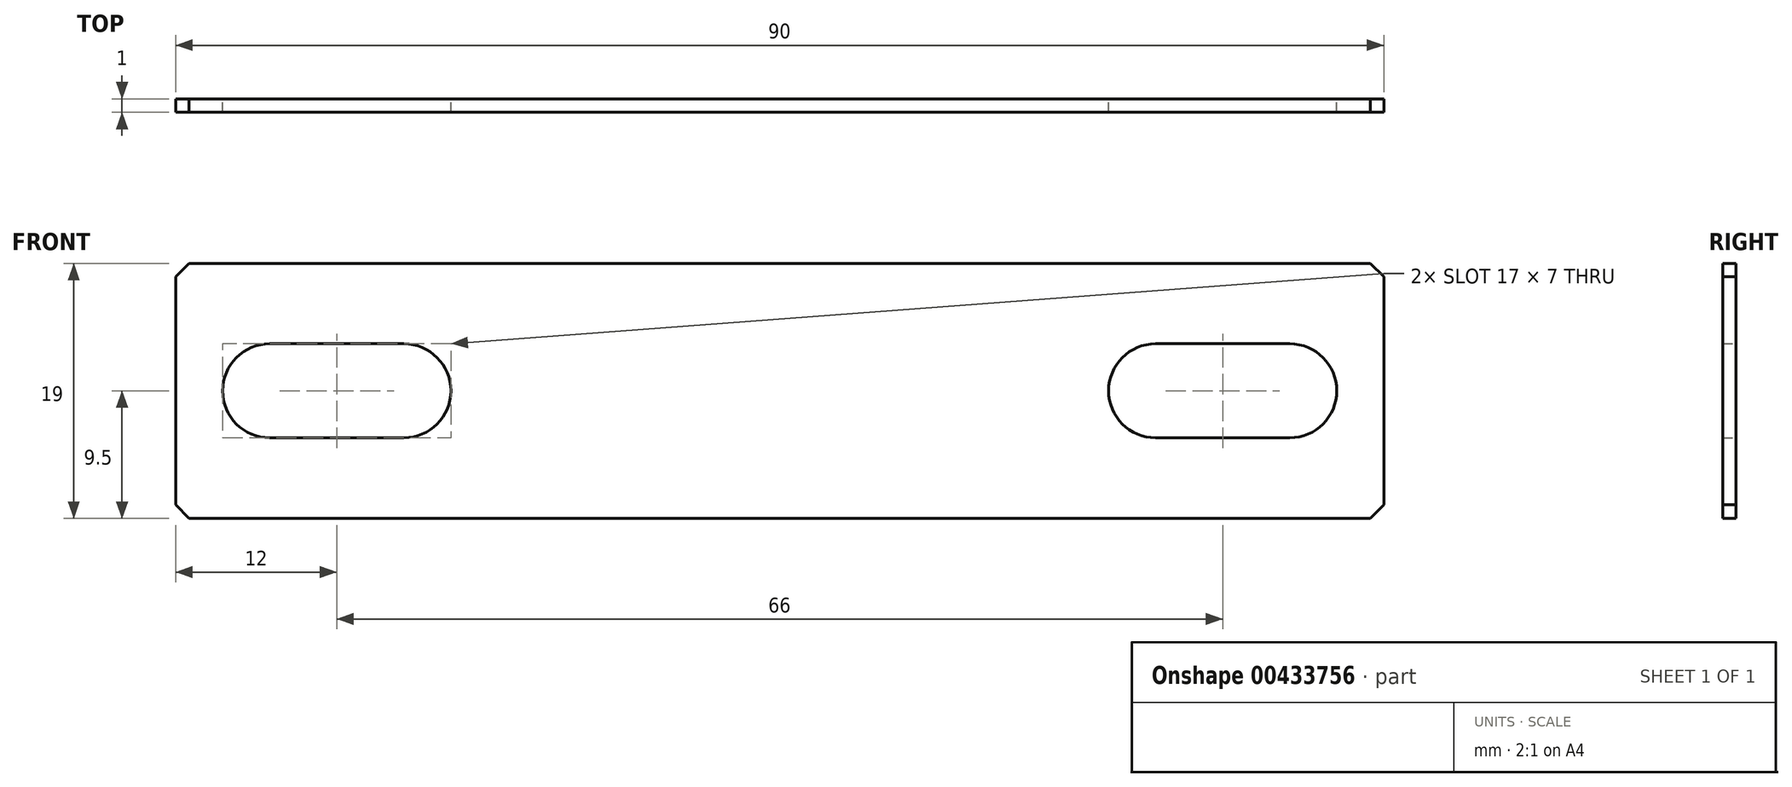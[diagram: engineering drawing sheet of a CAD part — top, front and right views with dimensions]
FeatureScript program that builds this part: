
annotation { "Feature Type Name" : "Feature", "Feature Type Description" : "" }
export const myFeature = defineFeature(function(context is Context, id is Id, definition is map)
    precondition{}
    {
        {
            var Q0;
            Q0=qCreatedBy(makeId("Front.planeOp"),FACE);
            var sketch = newSketch(context, id + "F0", { "sketchPlane" : qUnion([Q0])});
            skLineSegment(sketch, "E0", {"start": v(0, 0) * mm, "end": v(0, 19) * mm});
            skLineSegment(sketch, "E1", {"start": v(0, 0) * mm, "end": v(90, 0) * mm});
            skLineSegment(sketch, "E2.0", {"start": v(90, 0) * mm, "end": v(90, 19) * mm});
            skLineSegment(sketch, "E3.0", {"start": v(0, 19) * mm, "end": v(90, 19) * mm});
            skLineSegment(sketch, "E4.0", {"start": v(7, 6) * mm, "end": v(17, 6) * mm});
            skLineSegment(sketch, "E5.0", {"start": v(7, 13) * mm, "end": v(17, 13) * mm});
            skArc(sketch, "E6", {"start": v(83, 6) * mm, "mid": v(86.5, 9.5) * mm, "end": v(83, 13) * mm});
            skArc(sketch, "E7.MirrorCS", {"start": v(73, 6) * mm, "mid": v(69.5, 9.5) * mm, "end": v(73, 13) * mm});
            skLineSegment(sketch, "E8.trimOffspring", {"start": v(73, 13) * mm, "end": v(83, 13) * mm});
            skLineSegment(sketch, "E9.trimOffspring", {"start": v(73, 6) * mm, "end": v(83, 6) * mm});
            skArc(sketch, "E10.MirrorCS", {"start": v(17, 6) * mm, "mid": v(20.5, 9.5) * mm, "end": v(17, 13) * mm});
            skLineSegment(sketch, "E11.MirrorCS", {"start": v(17, 13) * mm, "end": v(7, 13) * mm});
            skLineSegment(sketch, "E12.MirrorCS", {"start": v(17, 6) * mm, "end": v(7, 6) * mm});
            skArc(sketch, "E13.MirrorCS", {"start": v(7, 6) * mm, "mid": v(3.5, 9.5) * mm, "end": v(7, 13) * mm});
            skSolve(sketch);
        }
        {
            var Q0;
            Q0 = qSketchRegion(id + "F0", true);
            extrude(context, id + "F1", {"entities" : qUnion([Q0]), "depth" : 1 * mm});
        }
        {
            var Q0;
            Q0=makeQuery(id+"F1.opExtrude","SWEPT_EDGE",EDGE,{"disambiguationData":[OSD([sQuery(id+"F0.wireOp",EDGE,"E2.0"),sQuery(id+"F0.wireOp",EDGE,"E3.0")])]});
            chamfer(context, id + "F2", {"entities" : qUnion([Q0]), "width" : 1 * mm, "tangentPropagation" : true});
        }
        {
            var Q0;
            Q0=makeQuery(id+"F1.opExtrude","SWEPT_EDGE",EDGE,{"disambiguationData":[OSD([sQuery(id+"F0.wireOp",EDGE,"E1"),sQuery(id+"F0.wireOp",EDGE,"E2.0")])]});
            chamfer(context, id + "F3", {"entities" : qUnion([Q0]), "width" : 1 * mm, "tangentPropagation" : true});
        }
        {
            var Q0;
            Q0=makeQuery(id+"F1.opExtrude","SWEPT_EDGE",EDGE,{"disambiguationData":[OSD([sQuery(id+"F0.wireOp",EDGE,"E0"),sQuery(id+"F0.wireOp",EDGE,"E3.0")])]});
            chamfer(context, id + "F4", {"entities" : qUnion([Q0]), "width" : 1 * mm, "tangentPropagation" : true});
        }
        {
            var Q0;
            Q0=makeQuery(id+"F1.opExtrude","SWEPT_EDGE",EDGE,{"disambiguationData":[OSD([sQuery(id+"F0.wireOp",EDGE,"E0"),sQuery(id+"F0.wireOp",EDGE,"E1")])]});
            chamfer(context, id + "F5", {"entities" : qUnion([Q0]), "width" : 1 * mm, "tangentPropagation" : true});
        }
    });
